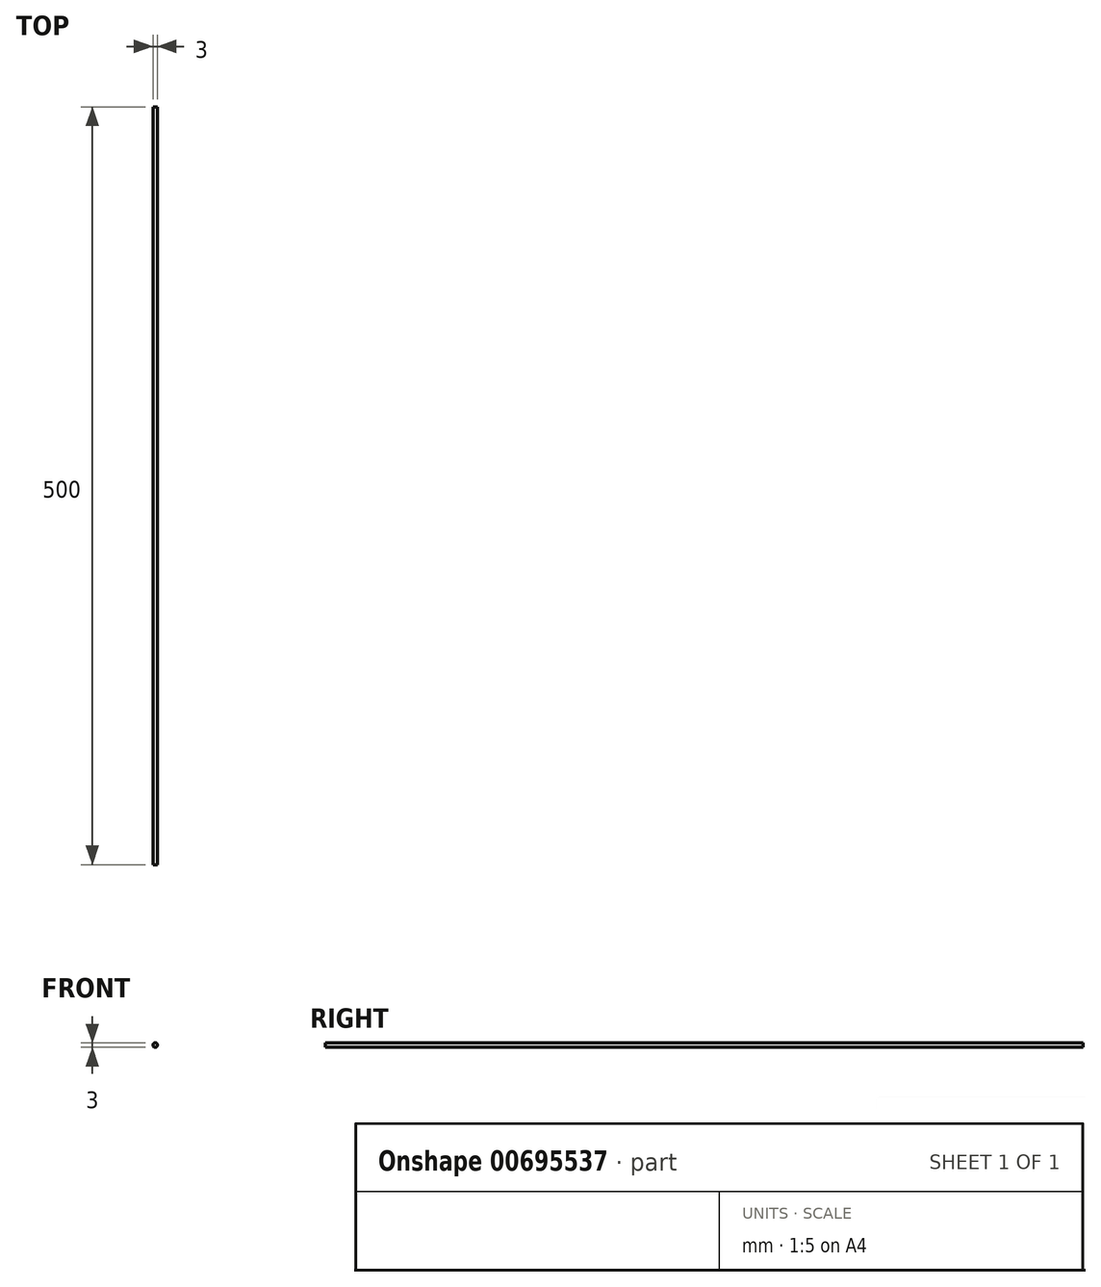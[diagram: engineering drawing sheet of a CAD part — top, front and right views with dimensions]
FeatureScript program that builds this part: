
annotation { "Feature Type Name" : "Feature", "Feature Type Description" : "" }
export const myFeature = defineFeature(function(context is Context, id is Id, definition is map)
    precondition{}
    {
        {
            var Q0;
            Q0=qCreatedBy(makeId("Front.planeOp"),FACE);
            var sketch = newSketch(context, id + "F0", { "sketchPlane" : qUnion([Q0])});
            skCircle(sketch, "E0", {"center": v(0, 0) * mm, "radius": 1.5 * mm});
            skSolve(sketch);
        }
        {
            var Q0;
            Q0=makeQuery(id+"F0.imprint","IMPRINT",FACE,{"disambiguationData":[TD([[makeQuery(id+"F0.imprint","IMPRINT",EDGE,{"derivedFrom":sQuery(id+"F0.wireOp",EDGE,"E0")}),1.0]])]});
            extrude(context, id + "F1", {"entities" : qUnion([Q0]), "endBound" : BoundingType.SYMMETRIC, "depth" : 500 * mm, "offsetDistance" : 25 * mm});
        }
    });
